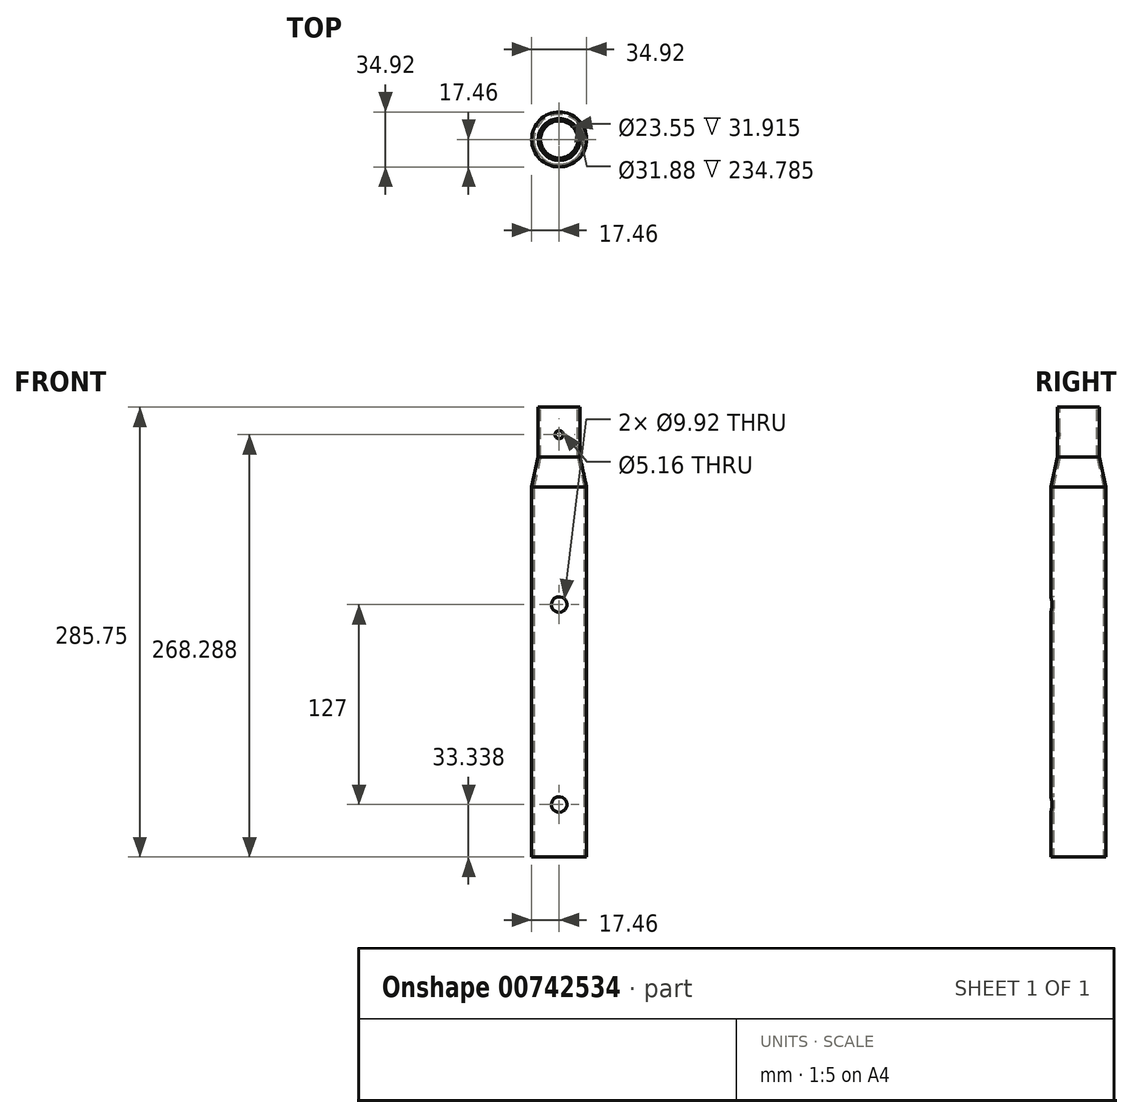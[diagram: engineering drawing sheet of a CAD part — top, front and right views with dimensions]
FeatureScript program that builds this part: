
annotation { "Feature Type Name" : "Feature", "Feature Type Description" : "" }
export const myFeature = defineFeature(function(context is Context, id is Id, definition is map)
    precondition{}
    {
        {
            var Q0;
            Q0=qCreatedBy(makeId("Top.planeOp"),FACE);
            var sketch = newSketch(context, id + "F0", { "sketchPlane" : qUnion([Q0])});
            skCircle(sketch, "E0", {"center": v(0, 0) * mm, "radius": 13.3 * mm});
            skSolve(sketch);
        }
        {
            var Q0;
            Q0=makeQuery(id+"F0.imprint","IMPRINT",FACE,{"disambiguationData":[TD([[makeQuery(id+"F0.imprint","IMPRINT",EDGE,{"derivedFrom":sQuery(id+"F0.wireOp",EDGE,"E0")}),1.0]])]});
            extrude(context, id + "F1", {"entities" : qUnion([Q0]), "oppositeDirection" : true, "depth" : 31.75 * mm, "offsetDistance" : 25.4 * mm});
        }
        {
            var Q0;
            Q0=qCreatedBy(makeId("Top.planeOp"),FACE);
            cPlane(context, id + "F2", {"entities" : qUnion([Q0]), "cplaneType" : CPlaneType.OFFSET, "offset" : 285.75 * mm, "oppositeDirection" : true, "width" : 152.4 * mm, "height" : 152.4 * mm});
        }
        {
            var Q0;
            Q0=qCreatedBy(id+"F2.planeOp",FACE);
            var sketch = newSketch(context, id + "F3", { "sketchPlane" : qUnion([Q0])});
            skCircle(sketch, "E1", {"center": v(0, 0) * mm, "radius": 17.46 * mm});
            skSolve(sketch);
        }
        {
            var Q0;
            Q0=makeQuery(id+"F3.imprint","IMPRINT",FACE,{"disambiguationData":[TD([[makeQuery(id+"F3.imprint","IMPRINT",EDGE,{"derivedFrom":sQuery(id+"F3.wireOp",EDGE,"E1")}),1.0]])]});
            extrude(context, id + "F4", {"entities" : qUnion([Q0]), "depth" : 234.95 * mm, "offsetDistance" : 25.4 * mm});
        }
        {
            var Q0;
            Q0=makeQuery(id+"F4.opExtrude","CAP_FACE",FACE,{"disambiguationData":[OSD([sQuery(id+"F3.wireOp",EDGE,"E1")])],"isStart":false});
            var Q1;
            Q1=makeQuery(id+"F1.opExtrude","CAP_FACE",FACE,{"disambiguationData":[OSD([sQuery(id+"F0.wireOp",EDGE,"E0")])],"isStart":false});
            loft(context, id + "F5", {"operationType" : NewBodyOperationType.ADD, "sheetProfilesArray" : [{ "sheetProfileEntities" : qUnion([Q0]) }, { "sheetProfileEntities" : qUnion([Q1]) }]});
        }
        {
            var Q0;
            Q0=makeQuery(id+"F1.opExtrude","CAP_FACE",FACE,{"disambiguationData":[OSD([sQuery(id+"F0.wireOp",EDGE,"E0")])],"isStart":true});
            var Q1;
            Q1=makeQuery(id+"F4.opExtrude","CAP_FACE",FACE,{"disambiguationData":[OSD([sQuery(id+"F3.wireOp",EDGE,"E1")])],"isStart":true});
            var Q2;
            Q2=makeQuery(id+"F1.opExtrude","SWEPT_BODY",BODY,{"disambiguationData":[OSD([sQuery(id+"F0.wireOp",EDGE,"E0")])]});
            shell(context, id + "F6", {"entities" : qUnion([Q0, Q1]), "parts" : qUnion([Q2]), "thickness" : 1.52 * mm});
        }
        {
            var Q0;
            Q0=qCreatedBy(makeId("Front.planeOp"),FACE);
            var sketch = newSketch(context, id + "F7", { "sketchPlane" : qUnion([Q0])});
            skPoint(sketch, "E2", {"position": v(0, -252.41) * mm});
            skPoint(sketch, "E3", {"position": v(0, -125.41) * mm});
            skPoint(sketch, "E4", {"position": v(0, -17.46) * mm});
            skSolve(sketch);
        }
        {
            var Q0;
            Q0=qCreatedBy(makeId("Front.planeOp"),FACE);
            cPlane(context, id + "F8", {"entities" : qUnion([Q0]), "cplaneType" : CPlaneType.OFFSET, "offset" : 17.46 * mm, "width" : 152.4 * mm, "height" : 152.4 * mm});
        }
        {
            var Q0;
            Q0=qCreatedBy(id+"F8.planeOp",FACE);
            var sketch = newSketch(context, id + "F9", { "sketchPlane" : qUnion([Q0])});
            skPoint(sketch, "E5", {"position": v(0, -252.41) * mm});
            skPoint(sketch, "E6", {"position": v(0, -125.41) * mm});
            skSolve(sketch);
        }
        {
            var Q0;
            Q0=qCreatedBy(makeId("Front.planeOp"),FACE);
            cPlane(context, id + "F10", {"entities" : qUnion([Q0]), "cplaneType" : CPlaneType.OFFSET, "offset" : 13.3 * mm, "width" : 152.4 * mm, "height" : 152.4 * mm});
        }
        {
            var Q0;
            Q0=qCreatedBy(id+"F10.planeOp",FACE);
            var sketch = newSketch(context, id + "F11", { "sketchPlane" : qUnion([Q0])});
            skPoint(sketch, "E7.0", {"position": v(0, -17.46) * mm});
            skSolve(sketch);
        }
        {
            var Q0;
            Q0=sQuery(id+"F9.wireOp",VERTEX,"E6");
            var Q1;
            Q1=sQuery(id+"F9.wireOp",VERTEX,"E5");
            var Q2;
            Q2=makeQuery(id+"F1.opExtrude","SWEPT_BODY",BODY,{"disambiguationData":[OSD([sQuery(id+"F0.wireOp",EDGE,"E0")])]});
            hole(context, id + "F12", {"style" : HoleStyle.SIMPLE, "endStyle" : HoleEndStyle.BLIND, "holeDiameter" : 9.92 * mm, "majorDiameter" : 6.35 * mm, "holeDepth" : 6.35 * mm, "isTappedThrough" : true, "tappedDepth" : 12.7 * mm, "tapClearance" : 3, "startFromSketch" : true, "locations" : qUnion([Q0, Q1]), "scope" : qUnion([Q2])});
        }
        {
            var Q0;
            Q0=sQuery(id+"F11.wireOp",VERTEX,"E7.0");
            var Q1;
            Q1=makeQuery(id+"F1.opExtrude","SWEPT_BODY",BODY,{"disambiguationData":[OSD([sQuery(id+"F0.wireOp",EDGE,"E0")])]});
            hole(context, id + "F13", {"style" : HoleStyle.SIMPLE, "endStyle" : HoleEndStyle.BLIND, "holeDiameter" : 5.16 * mm, "majorDiameter" : 6.35 * mm, "holeDepth" : 6.35 * mm, "isTappedThrough" : true, "tappedDepth" : 12.7 * mm, "tapClearance" : 3, "startFromSketch" : true, "locations" : qUnion([Q0]), "scope" : qUnion([Q1])});
        }
    });
